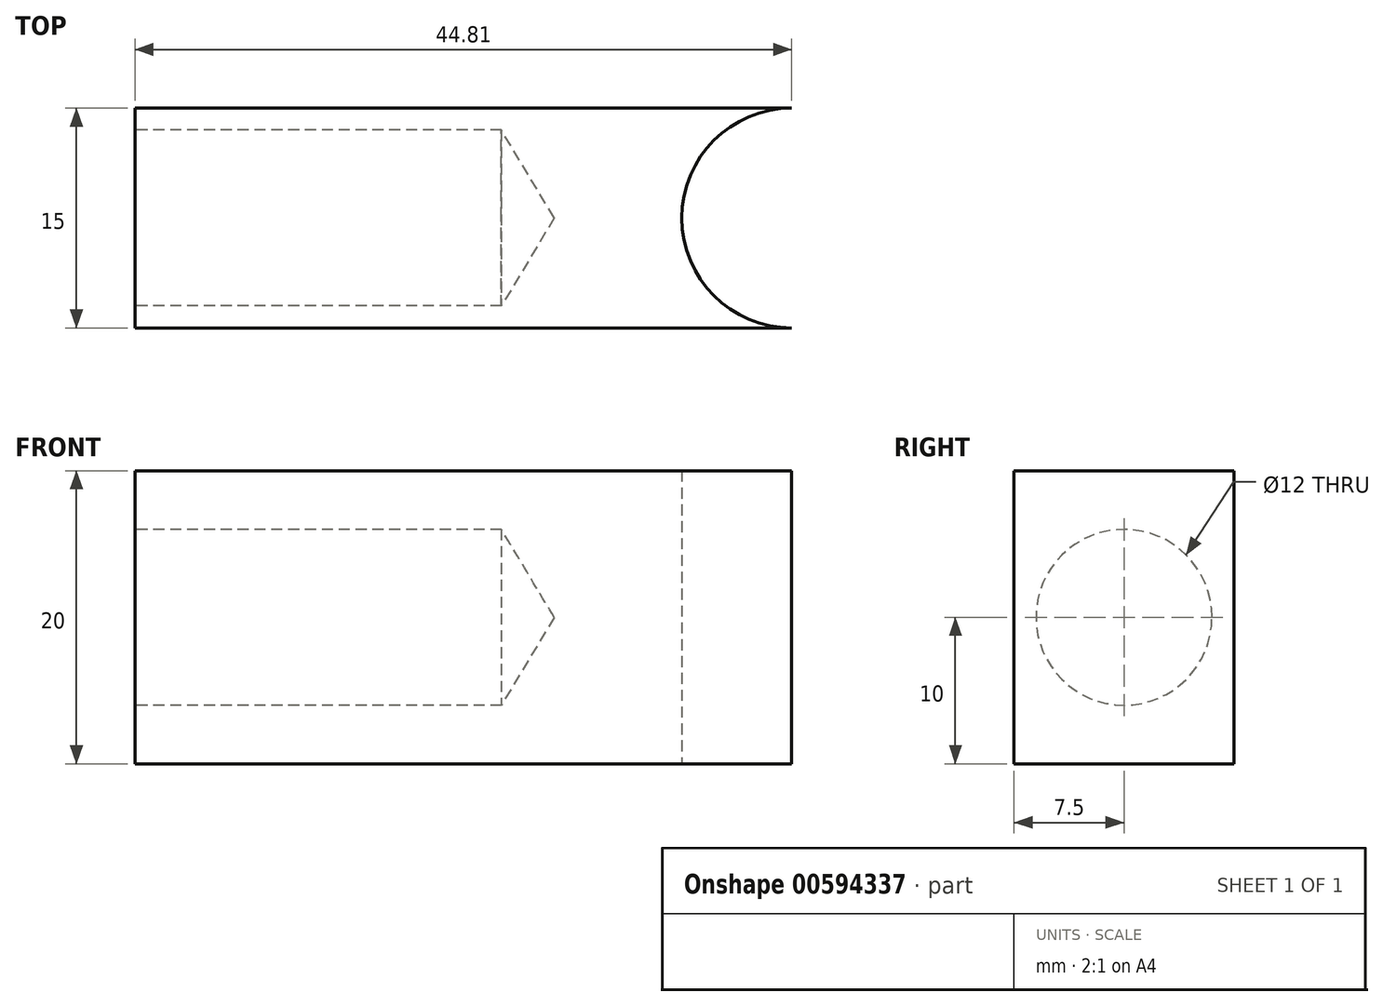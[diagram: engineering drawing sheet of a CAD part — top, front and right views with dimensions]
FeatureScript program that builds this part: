
annotation { "Feature Type Name" : "Feature", "Feature Type Description" : "" }
export const myFeature = defineFeature(function(context is Context, id is Id, definition is map)
    precondition{}
    {
        {
            var Q0;
            Q0=qCreatedBy(makeId("Top.planeOp"),FACE);
            var sketch = newSketch(context, id + "F0", { "sketchPlane" : qUnion([Q0])});
            skCircle(sketch, "E0", {"center": v(0, 0) * mm, "radius": 7.5 * mm});
            skLineSegment(sketch, "E1", {"start": v(0, -7.5) * mm, "end": v(-44.8, -7.5) * mm});
            skLineSegment(sketch, "E2", {"start": v(-44.8, -7.5) * mm, "end": v(-44.8, 7.5) * mm});
            skLineSegment(sketch, "E3", {"start": v(-44.8, 7.5) * mm, "end": v(0, 7.5) * mm});
            skSolve(sketch);
        }
        {
            var Q0;
            {var subQ0=sQuery(id+"F0.wireOp",EDGE,"E1");Q0=makeQuery(id+"F0.imprint","IMPRINT",FACE,{"disambiguationData":[TD([[makeQuery(id+"F0.imprint","IMPRINT",EDGE,{"derivedFrom":subQ0}),-1.0]])]});}
            extrude(context, id + "F1", {"entities" : qUnion([Q0]), "depth" : 20 * mm, "offsetDistance" : 25.4 * mm});
        }
        {
            var Q0;
            Q0=makeQuery(id+"F1.opExtrude","SWEPT_FACE",FACE,{"disambiguationData":[OSD([sQuery(id+"F0.wireOp",EDGE,"E2")])]});
            var sketch = newSketch(context, id + "F2", { "sketchPlane" : qUnion([Q0])});
            skCircle(sketch, "E4", {"center": v(0, 10) * mm, "radius": 6 * mm});
            skSolve(sketch);
        }
        {
            var Q0;
            Q0=sQuery(id+"F2.wireOp",VERTEX,"E4.center");
            var Q1;
            Q1=makeQuery(id+"F1.opExtrude","SWEPT_BODY",BODY,{"disambiguationData":[OSD([sQuery(id+"F0.wireOp",EDGE,"E0"),sQuery(id+"F0.wireOp",EDGE,"E1"),sQuery(id+"F0.wireOp",EDGE,"E2"),sQuery(id+"F0.wireOp",EDGE,"E3")])]});
            hole(context, id + "F3", {"style" : HoleStyle.SIMPLE, "endStyle" : HoleEndStyle.BLIND, "holeDiameter" : 12 * mm, "majorDiameter" : 6.35 * mm, "holeDepth" : 25 * mm, "isTappedThrough" : true, "tappedDepth" : 12.7 * mm, "tapClearance" : 3, "locations" : qUnion([Q0]), "scope" : qUnion([Q1])});
        }
    });
